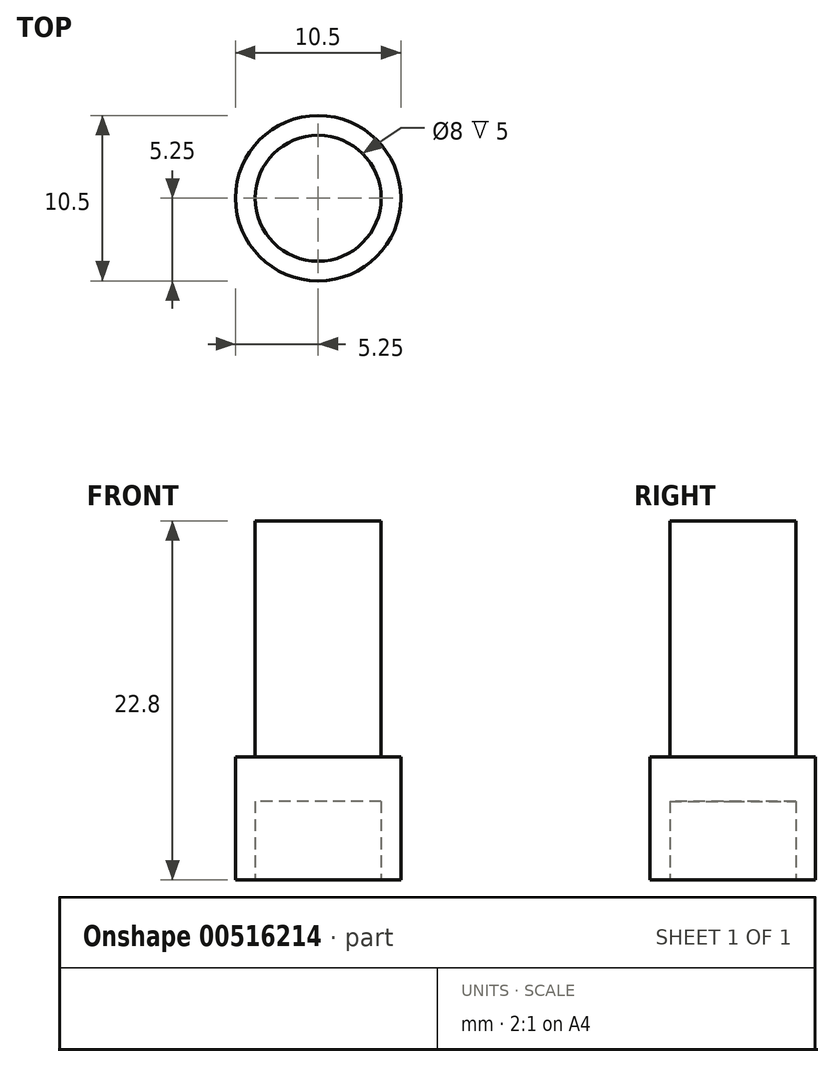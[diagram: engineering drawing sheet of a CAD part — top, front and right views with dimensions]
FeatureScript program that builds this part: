
annotation { "Feature Type Name" : "Feature", "Feature Type Description" : "" }
export const myFeature = defineFeature(function(context is Context, id is Id, definition is map)
    precondition{}
    {
        {
            var Q0;
            Q0=qCreatedBy(makeId("Top.planeOp"),FACE);
            var sketch = newSketch(context, id + "F0", { "sketchPlane" : qUnion([Q0])});
            skCircle(sketch, "E0", {"center": v(0, 0) * mm, "radius": 4 * mm});
            skCircle(sketch, "E1", {"center": v(0, 0) * mm, "radius": 5.25 * mm});
            skSolve(sketch);
        }
        {
            var Q0;
            Q0=makeQuery(id+"F0.imprint","IMPRINT",FACE,{"disambiguationData":[TD([[makeQuery(id+"F0.imprint","IMPRINT",EDGE,{"derivedFrom":sQuery(id+"F0.wireOp",EDGE,"E0")}),-1.0]])]});
            var Q1;
            Q1=makeQuery(id+"F0.imprint","IMPRINT",FACE,{"disambiguationData":[TD([[makeQuery(id+"F0.imprint","IMPRINT",EDGE,{"derivedFrom":sQuery(id+"F0.wireOp",EDGE,"E0")}),1.0]])]});
            extrude(context, id + "F1", {"entities" : qUnion([Q0, Q1]), "depth" : 7.8 * mm, "offsetDistance" : 25 * mm});
        }
        {
            var Q0;
            Q0=makeQuery(id+"F0.imprint","IMPRINT",FACE,{"disambiguationData":[TD([[makeQuery(id+"F0.imprint","IMPRINT",EDGE,{"derivedFrom":sQuery(id+"F0.wireOp",EDGE,"E0")}),1.0]])]});
            extrude(context, id + "F2", {"entities" : qUnion([Q0]), "operationType" : NewBodyOperationType.REMOVE, "depth" : 5 * mm, "offsetDistance" : 25 * mm});
        }
        {
            var Q0;
            Q0=makeQuery(id+"F1.opExtrude","CAP_FACE",FACE,{"disambiguationData":[OSD([sQuery(id+"F0.wireOp",EDGE,"E1")])],"isStart":false});
            var sketch = newSketch(context, id + "F3", { "sketchPlane" : qUnion([Q0])});
            skCircle(sketch, "E2", {"center": v(0, 0) * mm, "radius": 4 * mm});
            skSolve(sketch);
        }
        {
            var Q0;
            Q0=makeQuery(id+"F3.imprint","IMPRINT",FACE,{"disambiguationData":[TD([[makeQuery(id+"F3.imprint","IMPRINT",EDGE,{"derivedFrom":sQuery(id+"F3.wireOp",EDGE,"E2")}),1.0]])]});
            extrude(context, id + "F4", {"entities" : qUnion([Q0]), "operationType" : NewBodyOperationType.ADD, "depth" : 15 * mm, "offsetDistance" : 25 * mm});
        }
    });
